# Revit family: NEST_Basic_Tiltable_VIZULO
name_source: partatom
category: Lighting Fixtures
units: mm (PartAtom-declared; Revit-internal decimal feet)

## family parameters
Always vertical = Yes
Cut with Voids When Loaded = No
Light Source = Yes
OmniClass Number = 23.80.70.00
OmniClass Title = Lighting
Part Type = Normal
Room Calculation Point = No
Round Connector Dimension = Use Diameter
Shared = No
Work Plane-Based = No

## types (12) — shared parameters
Color Filter = 16777215
Dimming Lamp Color Temperature Shift = <None>
Emit Shape Visible in Rendering = No
Emit from Circle Diameter = 38 mm
Light Source Symbol Length = 3048 mm  [stored 10 ft]
Tilt Angle = 90.00°
zero-valued in all types: Default Elevation

## per-type parameters (varying)
| type | Spot Beam Angle | Spot Field Angle |
| 24°/8 W/3000 K | 24.00° | 24.00° |
| 24°/8 W/4000 K | 24.00° | 24.00° |
| 24°/12 W/3000 K | 24.00° | 24.00° |
| 24°/12 W/4000 K | 24.00° | 24.00° |
| 36°/8 W/3000 K | 36.00° | 36.00° |
| 36°/8 W/4000 K | 36.00° | 36.00° |
| 36°/12 W/3000 K | 36.00° | 36.00° |
| 36°/12 W/4000 K | 36.00° | 36.00° |
| 60°/8 W/3000 K | 60.00° | 60.00° |
| 60°/8 W/4000 K | 60.00° | 60.00° |
| 60°/12 W/3000 K | 60.00° | 60.00° |
| 60°/12 W/4000 K | 60.00° | 60.00° |

note: [stored X ft] marks values corroborated as IEEE doubles in the binary element streams (Revit-internal decimal feet)

## geometry (parser evidence)
native form markers: Sweep x3
no freeform markers — native parametric forms only
